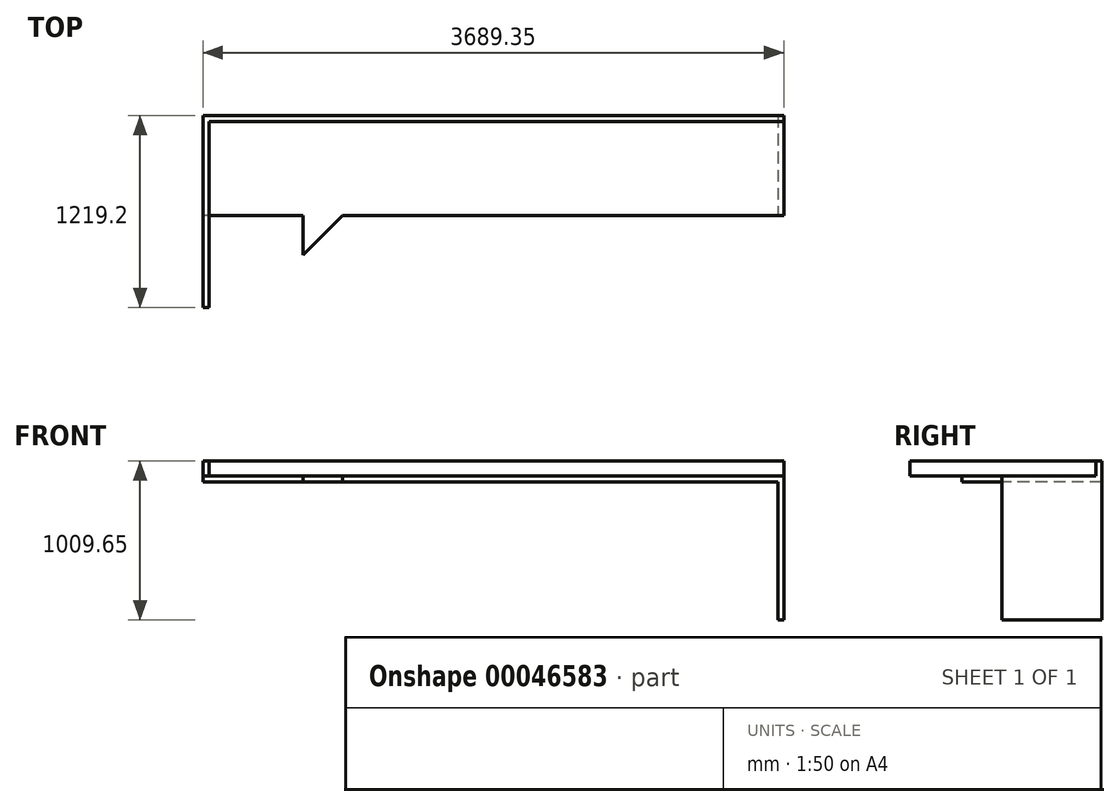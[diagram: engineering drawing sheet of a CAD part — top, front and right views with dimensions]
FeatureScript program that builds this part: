
annotation { "Feature Type Name" : "Feature", "Feature Type Description" : "" }
export const myFeature = defineFeature(function(context is Context, id is Id, definition is map)
    precondition{}
    {
        {
            var Q0;
            Q0=qCreatedBy(makeId("Top.planeOp"),FACE);
            var sketch = newSketch(context, id + "F0", { "sketchPlane" : qUnion([Q0])});
            skLineSegment(sketch, "E0.rect.bottom", {"start": v(1825.63, 317.5) * mm, "end": v(-1825.63, 317.5) * mm});
            skLineSegment(sketch, "E0.rect.top", {"start": v(1825.63, -317.5) * mm, "end": v(-1825.63, -317.5) * mm});
            skLineSegment(sketch, "E0.rect.left", {"start": v(1825.63, 317.5) * mm, "end": v(1825.63, -317.5) * mm});
            skLineSegment(sketch, "E0.rect.right", {"start": v(-1825.63, 317.5) * mm, "end": v(-1825.63, -317.5) * mm});
            skPoint(sketch, "E0.rect.middle", {"position": v(0, 0) * mm});
            skLineSegment(sketch, "E1.bottom", {"start": v(1825.63, 317.5) * mm, "end": v(1863.73, 317.5) * mm});
            skLineSegment(sketch, "E1.top", {"start": v(1825.63, -317.5) * mm, "end": v(1863.73, -317.5) * mm});
            skLineSegment(sketch, "E1.right", {"start": v(1863.73, 317.5) * mm, "end": v(1863.73, -317.5) * mm});
            skLineSegment(sketch, "E2.bottom", {"start": v(-1825.63, -317.5) * mm, "end": v(-1190.62, -317.5) * mm});
            skLineSegment(sketch, "E2.top", {"start": v(-1825.62, -901.7) * mm, "end": v(-1190.62, -901.7) * mm});
            skLineSegment(sketch, "E2.left", {"start": v(-1825.62, -317.5) * mm, "end": v(-1825.62, -901.7) * mm});
            skLineSegment(sketch, "E2.right", {"start": v(-1190.62, -317.5) * mm, "end": v(-1190.62, -901.7) * mm});
            skLineSegment(sketch, "E3", {"start": v(-1190.62, -568.95) * mm, "end": v(-939.18, -317.5) * mm});
            skSolve(sketch);
        }
        {
            var Q0;
            Q0=makeQuery(id+"F0.imprint","IMPRINT",FACE,{"disambiguationData":[TD([[makeQuery(id+"F0.imprint","IMPRINT",EDGE,{"derivedFrom":sQuery(id+"F0.wireOp",EDGE,"E0.rect.bottom")}),1.0]])]});
            var Q1;
            Q1=makeQuery(id+"F0.imprint","IMPRINT",FACE,{"disambiguationData":[TD([[makeQuery(id+"F0.imprint","IMPRINT",EDGE,{"derivedFrom":sQuery(id+"F0.wireOp",EDGE,"E2.bottom")}),-1.0]])]});
            var Q2;
            Q2=makeQuery(id+"F0.imprint","IMPRINT",FACE,{"disambiguationData":[TD([[makeQuery(id+"F0.imprint","IMPRINT",EDGE,{"derivedFrom":sQuery(id+"F0.wireOp",EDGE,"E1.bottom")}),-1.0]])]});
            var Q3;
            {var subQ3=sQuery(id+"F0.wireOp",EDGE,"E3");Q3=makeQuery(id+"F0.imprint","IMPRINT",FACE,{"disambiguationData":[TD([[makeQuery(id+"F0.imprint","IMPRINT",EDGE,{"derivedFrom":subQ3}),1.0]])]});}
            extrude(context, id + "F1", {"entities" : qUnion([Q0, Q1, Q2, Q3]), "depth" : 38.1 * mm});
        }
        {
            var Q0;
            Q0=makeQuery(id+"F0.imprint","IMPRINT",FACE,{"disambiguationData":[TD([[makeQuery(id+"F0.imprint","IMPRINT",EDGE,{"derivedFrom":sQuery(id+"F0.wireOp",EDGE,"E1.bottom")}),-1.0]])]});
            extrude(context, id + "F2", {"entities" : qUnion([Q0]), "operationType" : NewBodyOperationType.ADD, "oppositeDirection" : true, "depth" : 876.3 * mm});
        }
        {
            var Q0;
            Q0=makeQuery(id+"F1.opExtrude","CAP_FACE",FACE,{"disambiguationData":[OSD([sQuery(id+"F0.wireOp",EDGE,"E0.rect.bottom"),sQuery(id+"F0.wireOp",EDGE,"E0.rect.top"),sQuery(id+"F0.wireOp",EDGE,"E0.rect.right"),sQuery(id+"F0.wireOp",EDGE,"E1.bottom"),sQuery(id+"F0.wireOp",EDGE,"E1.top"),sQuery(id+"F0.wireOp",EDGE,"E1.right"),sQuery(id+"F0.wireOp",EDGE,"E2.top"),sQuery(id+"F0.wireOp",EDGE,"E2.left"),sQuery(id+"F0.wireOp",EDGE,"E2.right")])],"isStart":false});
            var sketch = newSketch(context, id + "F3", { "sketchPlane" : qUnion([Q0])});
            skLineSegment(sketch, "E4.bottom", {"start": v(-1825.62, -901.7) * mm, "end": v(-1787.53, -901.7) * mm});
            skLineSegment(sketch, "E4.top", {"start": v(-1825.63, 317.5) * mm, "end": v(-1787.53, 317.5) * mm});
            skLineSegment(sketch, "E4.left", {"start": v(-1825.62, -901.7) * mm, "end": v(-1825.63, 317.5) * mm});
            skLineSegment(sketch, "E4.right", {"start": v(-1787.53, -901.7) * mm, "end": v(-1787.53, 279.4) * mm});
            skLineSegment(sketch, "E5.bottom", {"start": v(-1825.63, 317.5) * mm, "end": v(1863.73, 317.5) * mm});
            skLineSegment(sketch, "E5.top", {"start": v(-1787.53, 279.4) * mm, "end": v(1863.73, 279.4) * mm});
            skLineSegment(sketch, "E5.left", {"start": v(-1825.63, 317.5) * mm, "end": v(-1825.63, 279.4) * mm});
            skLineSegment(sketch, "E5.right", {"start": v(1863.73, 317.5) * mm, "end": v(1863.73, 279.4) * mm});
            skSolve(sketch);
        }
        {
            var Q0;
            Q0 = qSketchRegion(id + "F3", true);
            extrude(context, id + "F4", {"entities" : qUnion([Q0]), "operationType" : NewBodyOperationType.ADD, "depth" : 95.25 * mm});
        }
    });
